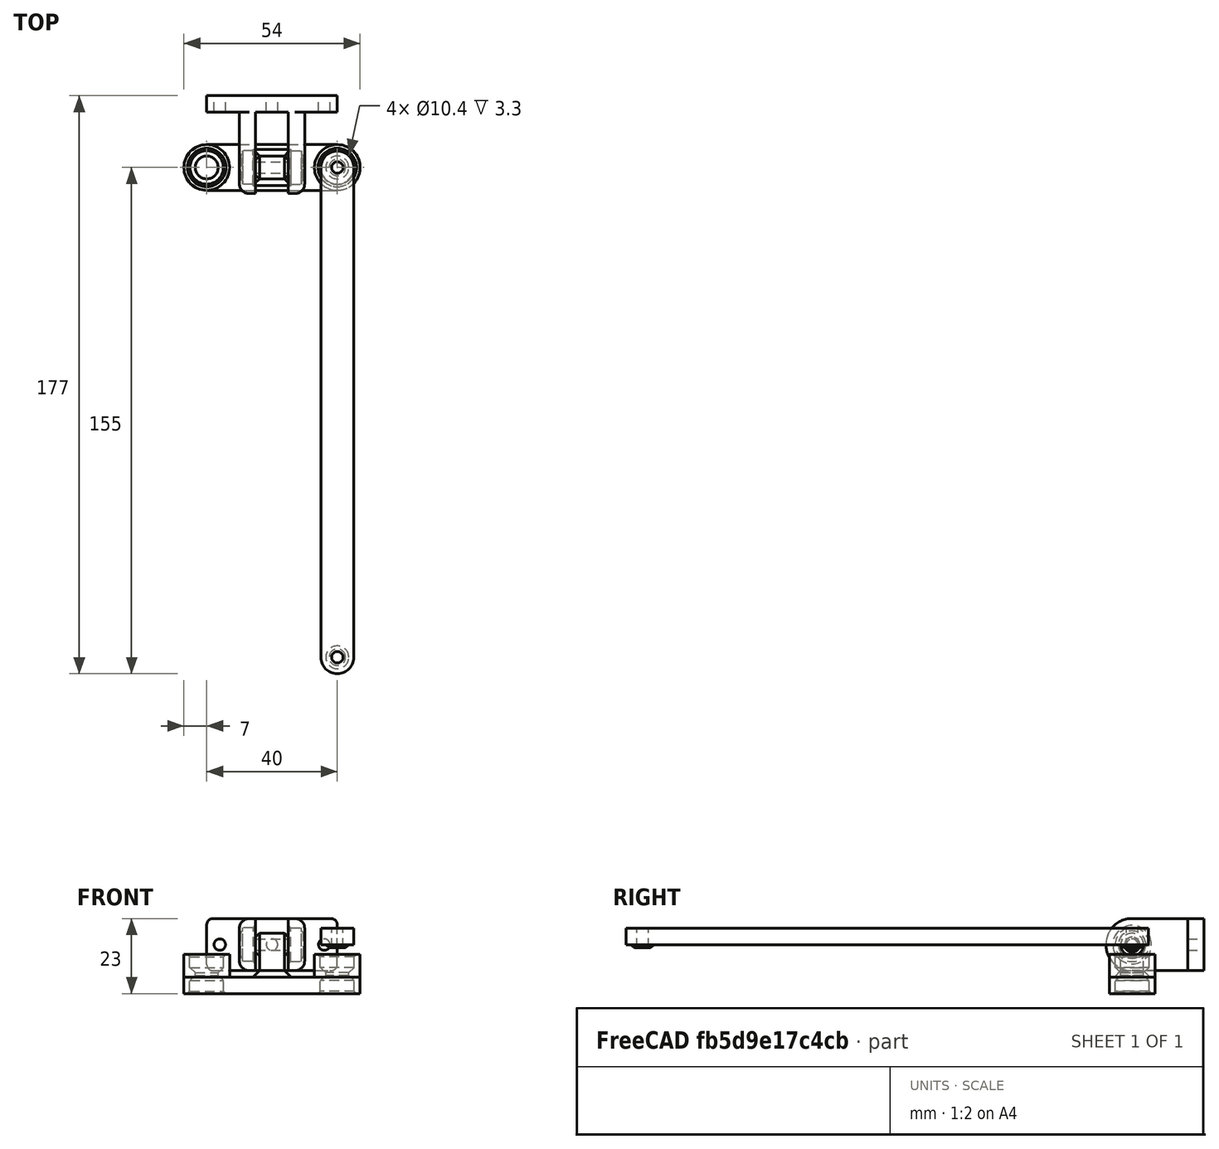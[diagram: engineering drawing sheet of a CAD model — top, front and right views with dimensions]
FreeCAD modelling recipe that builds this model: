
FCSTD DOCUMENT  (FreeCAD 0.19R24291 (Git))
Label: universal-joint-test
License: Other
LicenseURL: https://www.gnu.org/licenses/gpl-3.0.en.html
objects: Part::Cylinder×21, Part::MultiFuse×11, Part::Chamfer×8, Part::Fillet×7, Part::Box×6, Part::Cut×5, Part::Mirroring×3
note: 61 computed .brp shape members not serialized (recipe doc carries the construction recipe); baked Part::Feature solids carry a one-line shape summary decoded from their .brp

FEATURE [Part::Cylinder] Cylinder001  label="bearing 2"
  Angle = 360
  AttacherType = Attacher::AttachEngine3D
  Height = 5
  Placement = pos=(4,0,0) rot=(0,1,0;1.5708rad)
  Radius = 5.2
FEATURE [Part::Cylinder] Cylinder002  label="bearing 3"
  Angle = 360
  AttacherType = Attacher::AttachEngine3D
  Height = 5
  Placement = pos=(20,0,-7) rot=(0,0,1;0rad)
  Radius = 5.2
FEATURE [Part::Cylinder] Cylinder003  label="M3"
  Angle = 360
  AttacherType = Attacher::AttachEngine3D
  Height = 26
  Placement = pos=(-13,0,0) rot=(0,1,0;1.5708rad)
  Radius = 1.75
FEATURE [Part::Box] Box  label="Cube"
  AttacherType = Attacher::AttachEngine3D
  Height = 16
  Length = 5
  Placement = pos=(5,-8,-8) rot=(0,0,1;0rad)
  Width = 25
FEATURE [Part::Fillet] Fillet
  Base = -> Box
  Edges = 2 edges r=7.9: [Edge9,Edge10]
FEATURE [Part::Fillet] Fillet001
  Base = -> Fillet
  Edges = 5 edges r=3: [Edge7,Edge11,Edge13,Edge14,Edge16]
FEATURE [Part::Cylinder] Cylinder005  label="M004"
  Angle = 360
  AttacherType = Attacher::AttachEngine3D
  Height = 10
  Placement = pos=(-5,0,0) rot=(0,1,0;1.5708rad)
  Radius = 3.5
FEATURE [Part::Chamfer] Chamfer
  Base = -> Cylinder005
  Edges = 2 edges r=1.2: [Edge1,Edge3]
FEATURE [Part::Box] Box001  label="Cube001"
  AttacherType = Attacher::AttachEngine3D
  Height = 10
  Length = 7.6
  Placement = pos=(-3.8,-3.5,-10) rot=(0,0,1;0rad)
  Width = 7
FEATURE [Part::Box] Box002  label="Cube002"
  AttacherType = Attacher::AttachEngine3D
  Height = 5
  Length = 54
  Placement = pos=(-27,-7,-15) rot=(0,0,1;0rad)
  Width = 14
FEATURE [Part::Cylinder] Cylinder006  label="bearing 004"
  Angle = 360
  AttacherType = Attacher::AttachEngine3D
  Height = 7
  Placement = pos=(20,0,-10) rot=(0,0,1;0rad)
  Radius = 7
FEATURE [Part::Cylinder] Cylinder007  label="M3-2"
  Angle = 360
  AttacherType = Attacher::AttachEngine3D
  Height = 20
  Placement = pos=(-16,10,0) rot=(-1,0,0;1.5708rad)
  Radius = 1.75
FEATURE [Part::Cylinder] Cylinder008  label="bearing 005"
  Angle = 360
  AttacherType = Attacher::AttachEngine3D
  Height = 5
  Placement = pos=(20,0,-16) rot=(0,0,1;0rad)
  Radius = 5.2
FEATURE [Part::Cylinder] Cylinder009  label="bearing 006"
  Angle = 360
  AttacherType = Attacher::AttachEngine3D
  Height = 7
  Placement = pos=(20,0,-10) rot=(0,0,1;0rad)
  Radius = 7
FEATURE [Part::Mirroring] Part__Mirroring  label="bearing 006 (Mirror #1)"
  Base = (0,0,0)
  Normal = (1,0,0)
  Source = -> Cylinder009
FEATURE [Part::Cylinder] Cylinder010  label="core"
  Angle = 360
  AttacherType = Attacher::AttachEngine3D
  Height = 20
  Placement = pos=(20,0,-20) rot=(0,0,1;0rad)
  Radius = 3.5
FEATURE [Part::Fillet] Fillet002
  Base = -> Box002
  Edges = 4 edges r=6.9: [Edge1,Edge3,Edge5,Edge7]
FEATURE [Part::MultiFuse] Fusion  label="bigrotate-1"
  Shapes = -> [Fillet002,Part__Mirroring,Cylinder006,Box001,Chamfer]
FEATURE [Part::MultiFuse] Fusion001  label="bearing-core"
  Shapes = -> [Cylinder010,Cylinder008,Cylinder002]
FEATURE [Part::Cylinder] Cylinder011  label="bearing 007"
  Angle = 360
  AttacherType = Attacher::AttachEngine3D
  Height = 5
  Placement = pos=(20,0,-7) rot=(0,0,1;0rad)
  Radius = 5.2
FEATURE [Part::Cylinder] Cylinder012  label="bearing 008"
  Angle = 360
  AttacherType = Attacher::AttachEngine3D
  Height = 5
  Placement = pos=(20,0,-16) rot=(0,0,1;0rad)
  Radius = 5.2
FEATURE [Part::Cylinder] Cylinder013  label="core001"
  Angle = 360
  AttacherType = Attacher::AttachEngine3D
  Height = 20
  Placement = pos=(20,0,-20) rot=(0,0,1;0rad)
  Radius = 3.5
FEATURE [Part::MultiFuse] Fusion002  label="bearing-core001"
  Shapes = -> [Cylinder013,Cylinder012,Cylinder011]
FEATURE [Part::Mirroring] Part__Mirroring001  label="bearing-core001 (Mirror #2)"
  Base = (0,0,0)
  Normal = (1,0,0)
  Source = -> Fusion002
FEATURE [Part::MultiFuse] Fusion003  label="bearing-cores"
  Shapes = -> [Fusion001,Part__Mirroring001]
FEATURE [Part::MultiFuse] Fusion004  label="big-holes"
  Shapes = -> [Cylinder003,Fusion003]
FEATURE [Part::Cut] Cut
  Base = -> Fusion
  Tool = -> Fusion004
FEATURE [Part::Chamfer] Chamfer001
  Base = -> Cut
  Edges = 4 edges r=1.6: [Edge67,Edge77,Edge78,Edge79]
FEATURE [Part::Chamfer] Chamfer002
  Base = -> Chamfer001
  Edges = 4 edges r=2: [Edge23,Edge24,Edge25,Edge26]
FEATURE [Part::Chamfer] Chamfer003  label="bigrotate"
  Base = -> Chamfer002
  Edges = 4 edges r=0.7: [Edge51,Edge52,Edge61,Edge66]
FEATURE [Part::Cylinder] Cylinder014  label="bearing 009"
  Angle = 360
  AttacherType = Attacher::AttachEngine3D
  Height = 13
  Placement = pos=(4,0,0) rot=(0,1,0;1.5708rad)
  Radius = 3.5
FEATURE [Part::Box] Box003  label="Cube003"
  AttacherType = Attacher::AttachEngine3D
  Height = 16
  Length = 40
  Placement = pos=(-20,17,-8) rot=(0,0,1;0rad)
  Width = 5
FEATURE [Part::MultiFuse] Fusion005  label="bearing-hole"
  Shapes = -> [Cylinder014,Cylinder001]
FEATURE [Part::Cut] Cut001  label="bearing-support-1"
  Base = -> Fillet001
  Tool = -> Fusion005
FEATURE [Part::Cylinder] Cylinder015  label="bearing 010"
  Angle = 360
  AttacherType = Attacher::AttachEngine3D
  Height = 5
  Placement = pos=(4,0,0) rot=(0,1,0;1.5708rad)
  Radius = 5.2
FEATURE [Part::Box] Box004  label="Cube004"
  AttacherType = Attacher::AttachEngine3D
  Height = 16
  Length = 5
  Placement = pos=(5,-8,-8) rot=(0,0,1;0rad)
  Width = 25
FEATURE [Part::Fillet] Fillet003
  Base = -> Box004
  Edges = 2 edges r=7.9: [Edge9,Edge10]
FEATURE [Part::Fillet] Fillet004
  Base = -> Fillet003
  Edges = 5 edges r=3: [Edge7,Edge11,Edge13,Edge14,Edge16]
FEATURE [Part::Cylinder] Cylinder016  label="bearing 011"
  Angle = 360
  AttacherType = Attacher::AttachEngine3D
  Height = 13
  Placement = pos=(4,0,0) rot=(0,1,0;1.5708rad)
  Radius = 3.5
FEATURE [Part::MultiFuse] Fusion006  label="bearing-hole001"
  Shapes = -> [Cylinder016,Cylinder015]
FEATURE [Part::Cut] Cut002  label="bearing-support-002"
  Base = -> Fillet004
  Tool = -> Fusion006
FEATURE [Part::Mirroring] Part__Mirroring002  label="bearing-support-002 (Mirror #3)"
  Base = (0,0,0)
  Normal = (1,0,0)
  Source = -> Cut002
FEATURE [Part::Cylinder] Cylinder017  label="M3-003"
  Angle = 360
  AttacherType = Attacher::AttachEngine3D
  Height = 20
  Placement = pos=(0,10,0) rot=(-1,0,0;1.5708rad)
  Radius = 1.75
FEATURE [Part::Cylinder] Cylinder018  label="M3-004"
  Angle = 360
  AttacherType = Attacher::AttachEngine3D
  Height = 20
  Placement = pos=(16,10,0) rot=(-1,0,0;1.5708rad)
  Radius = 1.75
FEATURE [Part::MultiFuse] Fusion007
  Shapes = -> [Cylinder007,Cylinder017,Cylinder018]
FEATURE [Part::MultiFuse] Fusion008  label="bearing-support-2"
  Shapes = -> [Cut001,Part__Mirroring002,Box003]
FEATURE [Part::Cut] Cut003
  Base = -> Fusion008
  Tool = -> Fusion007
FEATURE [Part::Fillet] Fillet005
  Base = -> Cut003
  Edges = 4 edges r=2: [Edge2,Edge4,Edge12,Edge22]
FEATURE [Part::Chamfer] Chamfer004
  Base = -> Fillet005
  Edges = 2 edges r=0.7: [Edge89,Edge95]
FEATURE [Part::Chamfer] Chamfer005  label="bracket"
  Base = -> Chamfer004
  Edges = 2 edges r=0.7: [Edge58,Edge110]
FEATURE [Part::Box] Box005  label="Cube005"
  AttacherType = Attacher::AttachEngine3D
  Height = 5
  Length = 10
  Placement = pos=(15,-144,0) rot=(0,0,1;0rad)
  Width = 160
FEATURE [Part::Fillet] Fillet006
  Base = -> Box005
  Edges = 4 edges r=4.9: [Edge1,Edge3,Edge5,Edge7]
  Placement = pos=(0,-11,0) rot=(0,0,1;0rad)
FEATURE [Part::Cylinder] Cylinder019  label="Cylinder"
  Angle = 360
  AttacherType = Attacher::AttachEngine3D
  Height = 10
  Placement = pos=(20,0,-2) rot=(0,0,1;0rad)
  Radius = 1.75
FEATURE [Part::Cylinder] Cylinder020
  Angle = 360
  AttacherType = Attacher::AttachEngine3D
  Height = 10
  Placement = pos=(20,-150,-2) rot=(0,0,1;0rad)
  Radius = 1.75
FEATURE [Part::Cylinder] Cylinder021
  Angle = 360
  AttacherType = Attacher::AttachEngine3D
  Height = 3
  Placement = pos=(20,0,-1) rot=(0,0,1;0rad)
  Radius = 3.5
FEATURE [Part::Chamfer] Chamfer006
  Base = -> Cylinder021
  Edges = 1 edges r=1: [Edge3]
FEATURE [Part::Cylinder] Cylinder022
  Angle = 360
  AttacherType = Attacher::AttachEngine3D
  Height = 2
  Placement = pos=(20,-150,-1) rot=(0,0,1;0rad)
  Radius = 3.5
FEATURE [Part::Chamfer] Chamfer007
  Base = -> Cylinder022
  Edges = 1 edges r=1: [Edge3]
FEATURE [Part::MultiFuse] Fusion009  label="rod-1"
  Shapes = -> [Fillet006,Chamfer006,Chamfer007]
FEATURE [Part::MultiFuse] Fusion010  label="rod-holes"
  Shapes = -> [Cylinder020,Cylinder019]
FEATURE [Part::Cut] Cut004  label="rod"
  Base = -> Fusion009
  Tool = -> Fusion010
